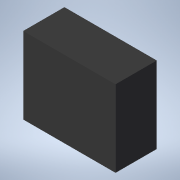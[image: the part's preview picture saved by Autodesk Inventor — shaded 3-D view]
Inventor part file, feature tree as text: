
AUTODESK INVENTOR PART (.ipt)
format: ipt  version: 2021 (Build 250183000, 183)  size: 102,400 bytes
history: native  units: mm
features: reference x5, other x3, extrude x2, sketch x2, chamfer x1
ambient origin geometry x8: Origin, YZ Plane, XZ Plane, XY Plane, X Axis, Y Axis, Z Axis, Center Point
bodies: Volumenkörper1 (feature_tree)
feature tree (13):
  extrude  "Extrusion1"  Depth=6.4mm TaperAngle=0.0deg
  extrude  "Extrusion2"  Depth=5.4mm TaperAngle=45.0deg
  chamfer  "Fase1"  [1 undecoded]
  sketch  "Skizze1"  dims[d0=3.35mm d1=6.4mm d2=0.0mm]
  reference  "Referenz1"
  reference  "Referenz2"
  reference  "Referenz3"
  reference  "Referenz4"
  reference  "Referenz5"
  sketch  "Skizze2"  dims[d3=5.4mm d4=0.0mm d5=0.6mm d6=2.0mm d7=45.0deg]
  other  "<userpath>\Desktop\Bachelorarbeit\CAD\00_RobotAssembly.iam"
  other  "00_RobotAssembly.iam"
  other  "12_Motor_Fixation:1"
note: 1 required parameter value undecoded (feature->parameter linkage not recoverable at this tier; creation-order binding heuristic only, values carry confidence <= 0.55)
